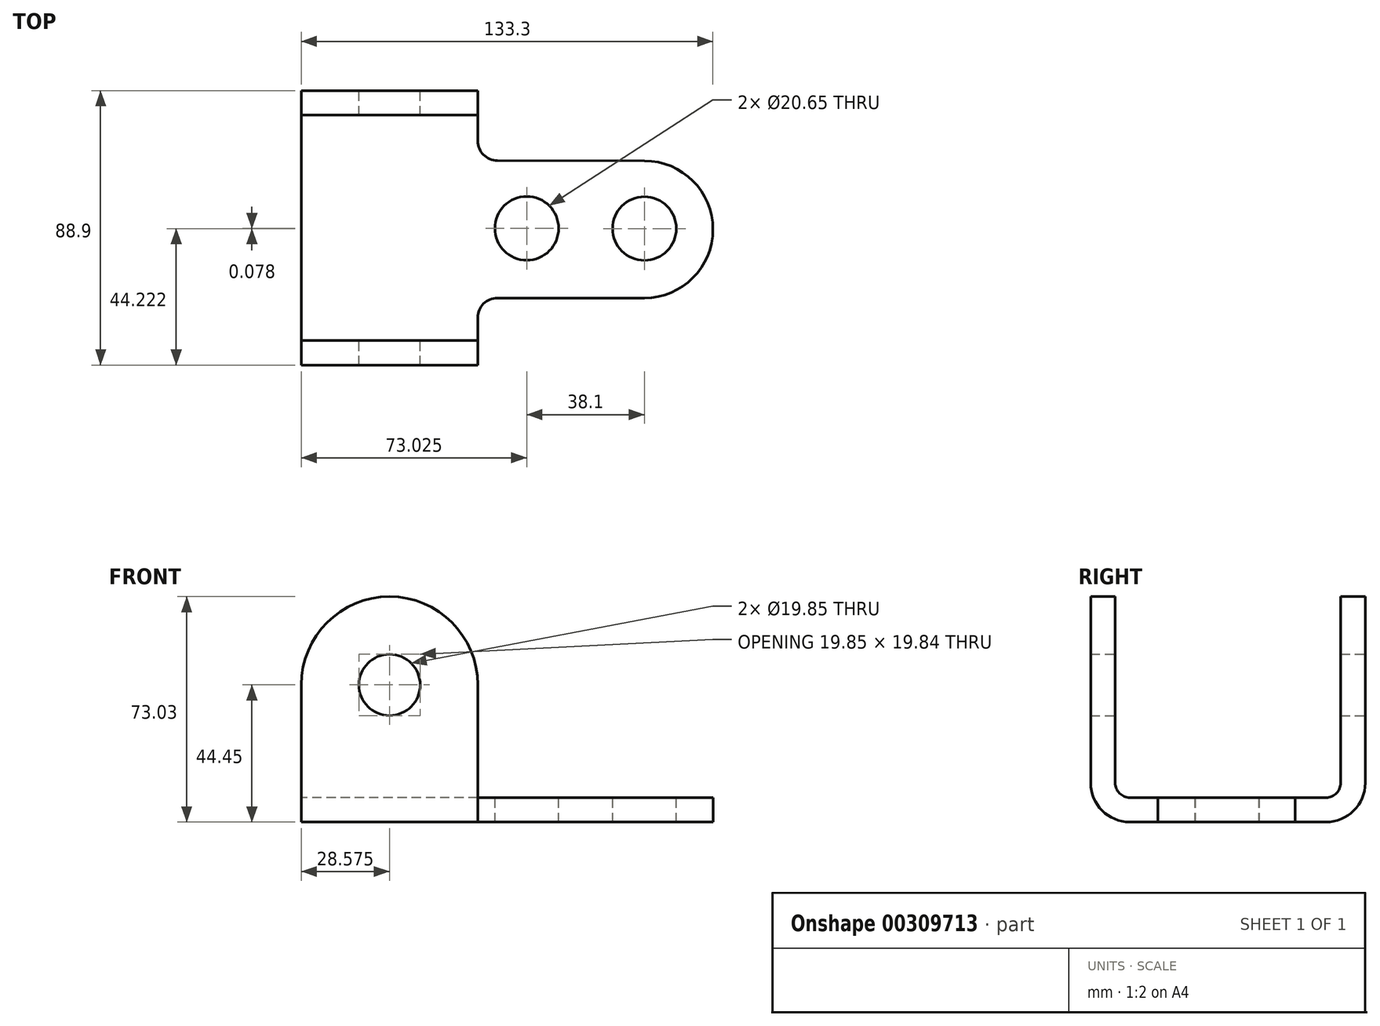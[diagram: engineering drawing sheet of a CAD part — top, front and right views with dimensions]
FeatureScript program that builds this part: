
annotation { "Feature Type Name" : "Feature", "Feature Type Description" : "" }
export const myFeature = defineFeature(function(context is Context, id is Id, definition is map)
    precondition{}
    {
        {
            var Q0;
            Q0=qCreatedBy(makeId("Front.planeOp"),FACE);
            var sketch = newSketch(context, id + "F0", { "sketchPlane" : qUnion([Q0])});
            skLineSegment(sketch, "E0", {"start": v(0, 0) * mm, "end": v(0, 44.45) * mm});
            skArc(sketch, "E1", {"start": v(0, 44.45) * mm, "mid": v(28.57, 73.03) * mm, "end": v(57.15, 44.45) * mm});
            skLineSegment(sketch, "E2", {"start": v(57.15, 44.45) * mm, "end": v(57.15, 0) * mm});
            skLineSegment(sketch, "E3", {"start": v(57.15, 0) * mm, "end": v(0, 0) * mm});
            skCircle(sketch, "E4", {"center": v(28.58, 44.45) * mm, "radius": 9.92 * mm});
            skSolve(sketch);
        }
        {
            var Q0;
            Q0 = qSketchRegion(id + "F0", true);
            extrude(context, id + "F1", {"entities" : qUnion([Q0]), "endBound" : BoundingType.SYMMETRIC, "depth" : 88.9 * mm});
        }
        {
            var Q0;
            Q0=qCreatedBy(makeId("Right.planeOp"),FACE);
            var sketch = newSketch(context, id + "F2", { "sketchPlane" : qUnion([Q0])});
            skLineSegment(sketch, "E5.bottom", {"start": v(36.53, 73.03) * mm, "end": v(-36.53, 73.03) * mm});
            skLineSegment(sketch, "E5.top", {"start": v(36.53, 0) * mm, "end": v(-36.53, 0) * mm});
            skLineSegment(sketch, "E5.left", {"start": v(36.53, 73.03) * mm, "end": v(36.53, 0) * mm});
            skLineSegment(sketch, "E5.right", {"start": v(-36.53, 73.03) * mm, "end": v(-36.53, 0) * mm});
            skLineSegment(sketch, "E6", {"start": v(36.53, 7.94) * mm, "end": v(-36.53, 7.94) * mm});
            skSolve(sketch);
        }
        {
            var Q0;
            {var subQ0=sQuery(id+"F2.wireOp",EDGE,"E5.bottom");Q0=makeQuery(id+"F2.imprint","IMPRINT",FACE,{"disambiguationData":[TD([[makeQuery(id+"F2.imprint","IMPRINT",EDGE,{"derivedFrom":subQ0}),1.0]])]});}
            extrude(context, id + "F3", {"entities" : qUnion([Q0]), "operationType" : NewBodyOperationType.REMOVE, "endBound" : BoundingType.THROUGH_ALL, "depth" : 25.4 * mm});
        }
        {
            var Q0;
            Q0=makeQuery(id+"F3.boolean.opBoolean","COPY",FACE,{"derivedFrom":makeQuery(id+"F3.opExtrude","SWEPT_FACE",FACE,{"disambiguationData":[OSD([sQuery(id+"F2.wireOp",EDGE,"E6")])]})});
            var sketch = newSketch(context, id + "F4", { "sketchPlane" : qUnion([Q0])});
            skArc(sketch, "E7", {"start": v(63.5, -22.71) * mm, "mid": v(59, -24.57) * mm, "end": v(57.15, -29.06) * mm});
            skLineSegment(sketch, "E8", {"start": v(63.5, -22.71) * mm, "end": v(111.12, -22.71) * mm});
            skLineSegment(sketch, "E9", {"start": v(0, 0) * mm, "end": v(238.17, -0.49) * mm, "construction": true});
            skLineSegment(sketch, "E10", {"start": v(111.12, 21.74) * mm, "end": v(63.5, 21.83) * mm});
            skArc(sketch, "E11", {"start": v(57.15, 28.18) * mm, "mid": v(59, 23.7) * mm, "end": v(63.5, 21.83) * mm});
            skLineSegment(sketch, "E12", {"start": v(57.15, 28.18) * mm, "end": v(57.15, 36.53) * mm});
            skLineSegment(sketch, "E13", {"start": v(57.15, 36.53) * mm, "end": v(0, 36.53) * mm});
            skLineSegment(sketch, "E14", {"start": v(0, 36.53) * mm, "end": v(0, 0) * mm});
            skLineSegment(sketch, "E15", {"start": v(0, -36.53) * mm, "end": v(57.15, -36.53) * mm});
            skLineSegment(sketch, "E16", {"start": v(57.15, -36.53) * mm, "end": v(57.15, -29.06) * mm});
            skCircle(sketch, "E17", {"center": v(73.03, -0.15) * mm, "radius": 10.33 * mm});
            skCircle(sketch, "E18", {"center": v(111.12, -0.23) * mm, "radius": 10.33 * mm});
            skLineSegment(sketch, "E19", {"start": v(57.15, 36.53) * mm, "end": v(57.15, -36.53) * mm});
            skArc(sketch, "E20", {"start": v(111.12, 21.74) * mm, "mid": v(133.3, -0.49) * mm, "end": v(111.12, -22.71) * mm});
            skSolve(sketch);
        }
        {
            var Q0;
            {var subQ1=sQuery(id+"F4.wireOp",EDGE,"E7");Q0=makeQuery(id+"F4.imprint","IMPRINT",FACE,{"disambiguationData":[TD([[makeQuery(id+"F4.imprint","IMPRINT",EDGE,{"derivedFrom":subQ1}),-1.0]])]});}
            extrude(context, id + "F5", {"entities" : qUnion([Q0]), "operationType" : NewBodyOperationType.ADD, "oppositeDirection" : true, "depth" : 7.94 * mm});
        }
        {
            var Q0;
            Q0=makeQuery(id+"F1.opExtrude","CAP_EDGE",EDGE,{"disambiguationData":[OSD([sQuery(id+"F0.wireOp",EDGE,"E3")])],"isStart":false});
            var Q1;
            Q1=makeQuery(id+"F1.opExtrude","CAP_EDGE",EDGE,{"disambiguationData":[OSD([sQuery(id+"F0.wireOp",EDGE,"E3")])],"isStart":true});
            fillet(context, id + "F6", {"entities" : qUnion([Q0, Q1]), "radius" : 12.7 * mm, "tangentPropagation" : true, "allowEdgeOverflow" : false});
        }
        {
            var Q0;
            Q0=makeQuery(id+"F3.boolean.opBoolean","COPY",EDGE,{"derivedFrom":makeQuery(id+"F3.opExtrude","SWEPT_EDGE",EDGE,{"disambiguationData":[OSD([sQuery(id+"F2.wireOp",EDGE,"E5.right"),sQuery(id+"F2.wireOp",EDGE,"E6")])]})});
            var Q1;
            Q1=makeQuery(id+"F3.boolean.opBoolean","COPY",EDGE,{"derivedFrom":makeQuery(id+"F3.opExtrude","SWEPT_EDGE",EDGE,{"disambiguationData":[OSD([sQuery(id+"F2.wireOp",EDGE,"E5.left"),sQuery(id+"F2.wireOp",EDGE,"E6")])]})});
            fillet(context, id + "F7", {"entities" : qUnion([Q0, Q1]), "radius" : 4.76 * mm, "tangentPropagation" : true, "allowEdgeOverflow" : false});
        }
    });
